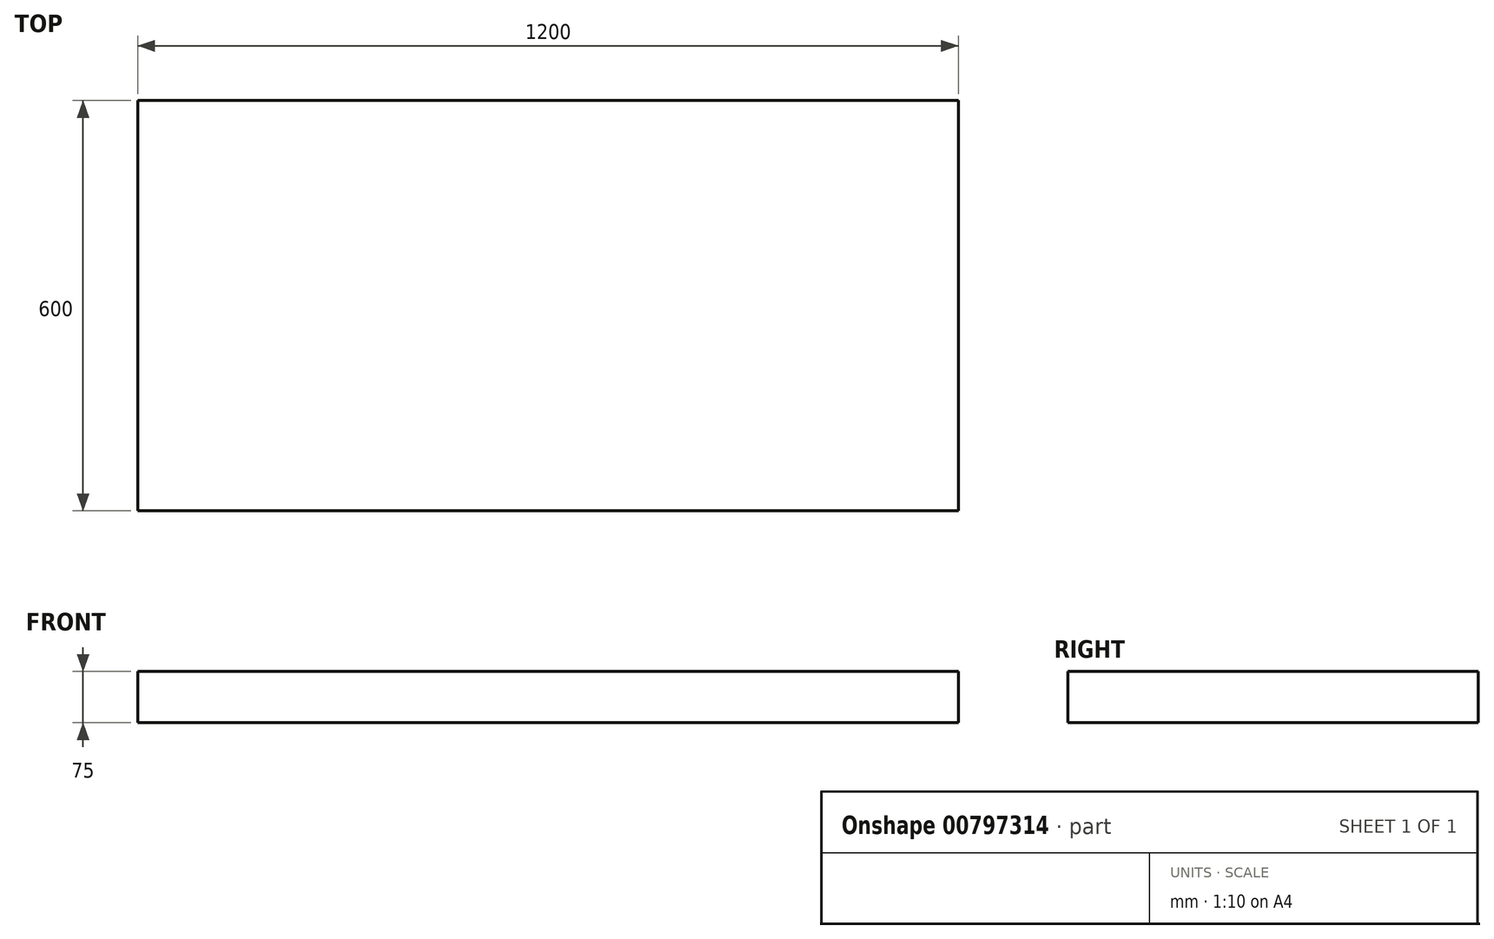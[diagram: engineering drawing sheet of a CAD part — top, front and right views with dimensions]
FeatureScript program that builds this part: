
annotation { "Feature Type Name" : "Feature", "Feature Type Description" : "" }
export const myFeature = defineFeature(function(context is Context, id is Id, definition is map)
    precondition{}
    {
        {
            var Q0;
            Q0=qCreatedBy(makeId("Top.planeOp"),FACE);
            var sketch = newSketch(context, id + "F0", { "sketchPlane" : qUnion([Q0])});
            skLineSegment(sketch, "E0.bottom", {"start": v(600, -300) * mm, "end": v(-600, -300) * mm});
            skLineSegment(sketch, "E0.top", {"start": v(600, 300) * mm, "end": v(-600, 300) * mm});
            skLineSegment(sketch, "E0.left", {"start": v(600, -300) * mm, "end": v(600, 300) * mm});
            skLineSegment(sketch, "E0.right", {"start": v(-600, -300) * mm, "end": v(-600, 300) * mm});
            skPoint(sketch, "E0.middle", {"position": v(0, 0) * mm});
            skSolve(sketch);
        }
        {
            var Q0;
            Q0 = qSketchRegion(id + "F0", true);
            extrude(context, id + "F1", {"entities" : qUnion([Q0]), "depth" : 75 * mm, "offsetDistance" : 25 * mm, "symmetric" : true});
        }
    });
